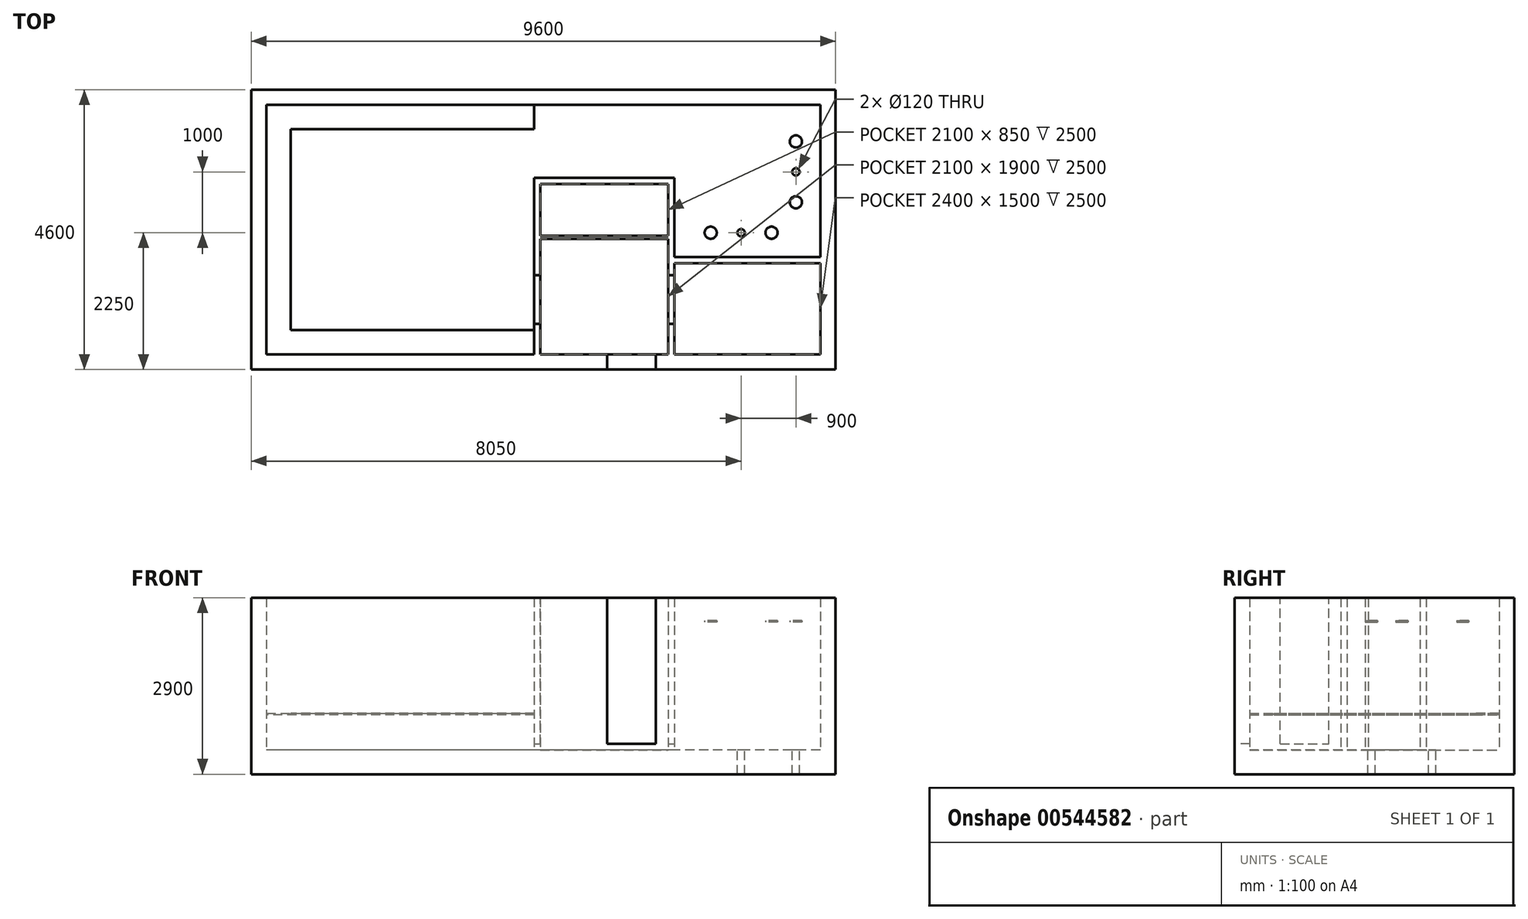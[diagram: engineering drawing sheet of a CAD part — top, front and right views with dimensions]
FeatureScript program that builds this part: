
annotation { "Feature Type Name" : "Feature", "Feature Type Description" : "" }
export const myFeature = defineFeature(function(context is Context, id is Id, definition is map)
    precondition{}
    {
        {
            var Q0;
            Q0=qCreatedBy(makeId("Top.planeOp"),FACE);
            var sketch = newSketch(context, id + "F0", { "sketchPlane" : qUnion([Q0])});
            skLineSegment(sketch, "E0.bottom", {"start": v(4550, -2050) * mm, "end": v(-4550, -2050) * mm});
            skLineSegment(sketch, "E0.top", {"start": v(4550, 2050) * mm, "end": v(-4550, 2050) * mm});
            skLineSegment(sketch, "E0.left", {"start": v(4550, -2050) * mm, "end": v(4550, 2050) * mm});
            skLineSegment(sketch, "E0.right", {"start": v(-4550, -2050) * mm, "end": v(-4550, 2050) * mm});
            skPoint(sketch, "E0.middle", {"position": v(0, 0) * mm});
            skLineSegment(sketch, "E1", {"start": v(2150, -2050) * mm, "end": v(2150, -550) * mm});
            skLineSegment(sketch, "E2", {"start": v(2150, -550) * mm, "end": v(4550, -550) * mm});
            skLineSegment(sketch, "E3", {"start": v(4550, -550) * mm, "end": v(4550, -450) * mm});
            skLineSegment(sketch, "E4", {"start": v(4550, -450) * mm, "end": v(2150, -450) * mm});
            skLineSegment(sketch, "E5", {"start": v(2150, -450) * mm, "end": v(2150, 850) * mm});
            skLineSegment(sketch, "E6", {"start": v(2150, 850) * mm, "end": v(2050, 850) * mm});
            skLineSegment(sketch, "E7", {"start": v(2050, 850) * mm, "end": v(2050, 850) * mm});
            skLineSegment(sketch, "E8", {"start": v(2050, 850) * mm, "end": v(-150, 850) * mm});
            skLineSegment(sketch, "E9", {"start": v(-150, 850) * mm, "end": v(-150, -2050) * mm});
            skLineSegment(sketch, "E10", {"start": v(-150, -2050) * mm, "end": v(-50, -2050) * mm});
            skLineSegment(sketch, "E11", {"start": v(-50, -2050) * mm, "end": v(-50, 750) * mm});
            skLineSegment(sketch, "E12", {"start": v(-50, 750) * mm, "end": v(2050, 750) * mm});
            skLineSegment(sketch, "E13", {"start": v(2050, 750) * mm, "end": v(2050, -2050) * mm});
            skLineSegment(sketch, "E14", {"start": v(2050, -2050) * mm, "end": v(2150, -2050) * mm});
            skLineSegment(sketch, "E15", {"start": v(2050, 750) * mm, "end": v(2050, 850) * mm});
            skCircle(sketch, "E16", {"center": v(2750, -50) * mm, "radius": 100 * mm, "construction": true});
            skCircle(sketch, "E17", {"center": v(3750, -50) * mm, "radius": 100 * mm, "construction": true});
            skCircle(sketch, "E18", {"center": v(4150, 450) * mm, "radius": 100 * mm, "construction": true});
            skLineSegment(sketch, "E19", {"start": v(2150, -50) * mm, "end": v(2750, -50) * mm, "construction": true});
            skLineSegment(sketch, "E20", {"start": v(3750, -50) * mm, "end": v(2750, -50) * mm, "construction": true});
            skLineSegment(sketch, "E21", {"start": v(4550, -50) * mm, "end": v(3750, -50) * mm, "construction": true});
            skLineSegment(sketch, "E22", {"start": v(3750, -50) * mm, "end": v(3750, -450) * mm, "construction": true});
            skLineSegment(sketch, "E23", {"start": v(4550, 450) * mm, "end": v(4150, 450) * mm, "construction": true});
            skCircle(sketch, "E24", {"center": v(4150, 1450) * mm, "radius": 100 * mm, "construction": true});
            skLineSegment(sketch, "E25", {"start": v(4150, 1450) * mm, "end": v(4150, 450) * mm, "construction": true});
            skLineSegment(sketch, "E26", {"start": v(4150, -450) * mm, "end": v(4150, 450) * mm, "construction": true});
            skPoint(sketch, "E26.startSnap0", {"position": v(4150, -50) * mm});
            skLineSegment(sketch, "E27", {"start": v(4150, 1450) * mm, "end": v(4150, 2050) * mm, "construction": true});
            skLineSegment(sketch, "E28.bottom", {"start": v(-4800, 2300) * mm, "end": v(4800, 2300) * mm});
            skLineSegment(sketch, "E28.top", {"start": v(-4800, -2300) * mm, "end": v(4800, -2300) * mm});
            skLineSegment(sketch, "E28.left", {"start": v(-4800, 2300) * mm, "end": v(-4800, -2300) * mm});
            skLineSegment(sketch, "E28.right", {"start": v(4800, 2300) * mm, "end": v(4800, -2300) * mm});
            skCircle(sketch, "E29", {"center": v(3250, -50) * mm, "radius": 60 * mm});
            skCircle(sketch, "E30", {"center": v(4150, 950) * mm, "radius": 60 * mm});
            skSolve(sketch);
        }
        {
            var Q0;
            {var subQ3=sQuery(id+"F0.wireOp",EDGE,"E1");Q0=makeQuery(id+"F0.imprint","IMPRINT",FACE,{"disambiguationData":[TD([[makeQuery(id+"F0.imprint","IMPRINT",EDGE,{"derivedFrom":subQ3}),-1.0]])]});}
            var Q1;
            {var subQ0=sQuery(id+"F0.wireOp",EDGE,"E11");Q1=makeQuery(id+"F0.imprint","IMPRINT",FACE,{"disambiguationData":[TD([[makeQuery(id+"F0.imprint","IMPRINT",EDGE,{"derivedFrom":subQ0}),-1.0]])]});}
            var Q2;
            {var subQ1=sQuery(id+"F0.wireOp",EDGE,"E0.left");var subQ3=sQuery(id+"F0.wireOp",EDGE,"E21");var subQ4=makeQuery(id+"F0.imprint","INTERSECT",VERTEX,{"derivedFrom":[subQ1,subQ3]});Q2=makeQuery(id+"F0.imprint","IMPRINT",FACE,{"disambiguationData":[TD([[makeQuery(id+"F0.imprint","IMPRINT",EDGE,{"disambiguationData":[TD([[subQ4,-1.0]])],"derivedFrom":subQ3}),1.0]])]});}
            var Q3;
            Q3=makeQuery(id+"F0.imprint","IMPRINT",FACE,{"disambiguationData":[TD([[makeQuery(id+"F0.imprint","IMPRINT",EDGE,{"derivedFrom":sQuery(id+"F0.wireOp",EDGE,"E8")}),1.0]])]});
            var Q4;
            {var subQ1=sQuery(id+"F0.wireOp",EDGE,"E0.left");var subQ6=sQuery(id+"F0.wireOp",EDGE,"E0.top");var subQ12=makeQuery(id+"F0.imprint","INTERSECT",VERTEX,{"derivedFrom":[subQ6,subQ1]});Q4=makeQuery(id+"F0.imprint","IMPRINT",FACE,{"disambiguationData":[TD([[makeQuery(id+"F0.imprint","IMPRINT",EDGE,{"disambiguationData":[TD([[subQ12,-1.0]])],"derivedFrom":subQ6}),1.0]])]});}
            var Q5;
            {var subQ1=sQuery(id+"F0.wireOp",EDGE,"E0.left");var subQ7=sQuery(id+"F0.wireOp",EDGE,"E21");var subQ8=makeQuery(id+"F0.imprint","INTERSECT",VERTEX,{"derivedFrom":[subQ1,subQ7]});Q5=makeQuery(id+"F0.imprint","IMPRINT",FACE,{"disambiguationData":[TD([[makeQuery(id+"F0.imprint","IMPRINT",EDGE,{"disambiguationData":[TD([[subQ8,-1.0]])],"derivedFrom":subQ1}),1.0]])]});}
            var Q6;
            Q6=makeQuery(id+"F0.imprint","IMPRINT",FACE,{"disambiguationData":[TD([[makeQuery(id+"F0.imprint","IMPRINT",EDGE,{"derivedFrom":sQuery(id+"F0.wireOp",EDGE,"E1")}),1.0]])]});
            var Q7;
            {var subQ9=sQuery(id+"F0.wireOp",EDGE,"E0.right");Q7=makeQuery(id+"F0.imprint","IMPRINT",FACE,{"disambiguationData":[TD([[makeQuery(id+"F0.imprint","IMPRINT",EDGE,{"derivedFrom":subQ9}),-1.0]])]});}
            var Q8;
            {var subQ9=sQuery(id+"F0.wireOp",EDGE,"E5");var subQ10=sQuery(id+"F0.wireOp",EDGE,"E4");var subQ11=makeQuery(id+"F0.imprint","INTERSECT",VERTEX,{"derivedFrom":[subQ10,subQ9]});Q8=makeQuery(id+"F0.imprint","IMPRINT",FACE,{"disambiguationData":[TD([[makeQuery(id+"F0.imprint","IMPRINT",EDGE,{"disambiguationData":[TD([[subQ11,1.0]])],"derivedFrom":subQ10}),-1.0]])]});}
            var Q9;
            {var subQ0=sQuery(id+"F0.wireOp",EDGE,"E19");var subQ1=sQuery(id+"F0.wireOp",EDGE,"E16");var subQ2=makeQuery(id+"F0.imprint","INTERSECT",VERTEX,{"derivedFrom":[subQ1,subQ0]});Q9=makeQuery(id+"F0.imprint","IMPRINT",FACE,{"disambiguationData":[TD([[makeQuery(id+"F0.imprint","IMPRINT",EDGE,{"disambiguationData":[TD([[subQ2,1.0]])],"derivedFrom":subQ1}),1.0]])]});}
            var Q10;
            {var subQ0=sQuery(id+"F0.wireOp",EDGE,"E19");var subQ1=sQuery(id+"F0.wireOp",EDGE,"E16");var subQ2=makeQuery(id+"F0.imprint","INTERSECT",VERTEX,{"derivedFrom":[subQ1,subQ0]});Q10=makeQuery(id+"F0.imprint","IMPRINT",FACE,{"disambiguationData":[TD([[makeQuery(id+"F0.imprint","IMPRINT",EDGE,{"disambiguationData":[TD([[subQ2,-1.0]])],"derivedFrom":subQ1}),1.0]])]});}
            var Q11;
            {var subQ0=sQuery(id+"F0.wireOp",EDGE,"E22");var subQ1=sQuery(id+"F0.wireOp",EDGE,"E4");var subQ2=makeQuery(id+"F0.imprint","INTERSECT",VERTEX,{"derivedFrom":[subQ1,subQ0]});Q11=makeQuery(id+"F0.imprint","IMPRINT",FACE,{"disambiguationData":[TD([[makeQuery(id+"F0.imprint","IMPRINT",EDGE,{"disambiguationData":[TD([[subQ2,1.0]])],"derivedFrom":subQ1}),-1.0]])]});}
            var Q12;
            {var subQ0=sQuery(id+"F0.wireOp",EDGE,"E25");var subQ1=sQuery(id+"F0.wireOp",EDGE,"E24");var subQ2=makeQuery(id+"F0.imprint","INTERSECT",VERTEX,{"derivedFrom":[subQ1,subQ0]});Q12=makeQuery(id+"F0.imprint","IMPRINT",FACE,{"disambiguationData":[TD([[makeQuery(id+"F0.imprint","IMPRINT",EDGE,{"disambiguationData":[TD([[subQ2,1.0]])],"derivedFrom":subQ1}),1.0]])]});}
            var Q13;
            {var subQ0=sQuery(id+"F0.wireOp",EDGE,"E25");var subQ1=sQuery(id+"F0.wireOp",EDGE,"E24");var subQ2=makeQuery(id+"F0.imprint","INTERSECT",VERTEX,{"derivedFrom":[subQ1,subQ0]});Q13=makeQuery(id+"F0.imprint","IMPRINT",FACE,{"disambiguationData":[TD([[makeQuery(id+"F0.imprint","IMPRINT",EDGE,{"disambiguationData":[TD([[subQ2,-1.0]])],"derivedFrom":subQ1}),1.0]])]});}
            var Q14;
            {var subQ0=sQuery(id+"F0.wireOp",EDGE,"E25");var subQ1=sQuery(id+"F0.wireOp",EDGE,"E18");var subQ2=makeQuery(id+"F0.imprint","INTERSECT",VERTEX,{"derivedFrom":[subQ1,subQ0]});Q14=makeQuery(id+"F0.imprint","IMPRINT",FACE,{"disambiguationData":[TD([[makeQuery(id+"F0.imprint","IMPRINT",EDGE,{"disambiguationData":[TD([[subQ2,-1.0]])],"derivedFrom":subQ1}),1.0]])]});}
            var Q15;
            {var subQ0=sQuery(id+"F0.wireOp",EDGE,"E25");var subQ1=sQuery(id+"F0.wireOp",EDGE,"E18");var subQ2=makeQuery(id+"F0.imprint","INTERSECT",VERTEX,{"derivedFrom":[subQ1,subQ0]});Q15=makeQuery(id+"F0.imprint","IMPRINT",FACE,{"disambiguationData":[TD([[makeQuery(id+"F0.imprint","IMPRINT",EDGE,{"disambiguationData":[TD([[subQ2,1.0]])],"derivedFrom":subQ1}),1.0]])]});}
            var Q16;
            {var subQ0=sQuery(id+"F0.wireOp",EDGE,"E21");var subQ1=sQuery(id+"F0.wireOp",EDGE,"E17");var subQ2=makeQuery(id+"F0.imprint","INTERSECT",VERTEX,{"derivedFrom":[subQ1,subQ0]});Q16=makeQuery(id+"F0.imprint","IMPRINT",FACE,{"disambiguationData":[TD([[makeQuery(id+"F0.imprint","IMPRINT",EDGE,{"disambiguationData":[TD([[subQ2,1.0]])],"derivedFrom":subQ1}),1.0]])]});}
            var Q17;
            {var subQ0=sQuery(id+"F0.wireOp",EDGE,"E20");var subQ1=sQuery(id+"F0.wireOp",EDGE,"E17");var subQ2=makeQuery(id+"F0.imprint","INTERSECT",VERTEX,{"derivedFrom":[subQ1,subQ0]});Q17=makeQuery(id+"F0.imprint","IMPRINT",FACE,{"disambiguationData":[TD([[makeQuery(id+"F0.imprint","IMPRINT",EDGE,{"disambiguationData":[TD([[subQ2,-1.0]])],"derivedFrom":subQ1}),1.0]])]});}
            var Q18;
            {var subQ0=sQuery(id+"F0.wireOp",EDGE,"E20");var subQ1=sQuery(id+"F0.wireOp",EDGE,"E17");var subQ2=makeQuery(id+"F0.imprint","INTERSECT",VERTEX,{"derivedFrom":[subQ1,subQ0]});Q18=makeQuery(id+"F0.imprint","IMPRINT",FACE,{"disambiguationData":[TD([[makeQuery(id+"F0.imprint","IMPRINT",EDGE,{"disambiguationData":[TD([[subQ2,1.0]])],"derivedFrom":subQ1}),1.0]])]});}
            var Q19;
            {var subQ0=sQuery(id+"F0.wireOp",EDGE,"E23");var subQ1=sQuery(id+"F0.wireOp",EDGE,"E18");var subQ2=makeQuery(id+"F0.imprint","INTERSECT",VERTEX,{"derivedFrom":[subQ1,subQ0]});Q19=makeQuery(id+"F0.imprint","IMPRINT",FACE,{"disambiguationData":[TD([[makeQuery(id+"F0.imprint","IMPRINT",EDGE,{"disambiguationData":[TD([[subQ2,1.0]])],"derivedFrom":subQ1}),1.0]])]});}
            var Q20;
            {var subQ0=sQuery(id+"F0.wireOp",EDGE,"E0.right");Q20=makeQuery(id+"F0.imprint","IMPRINT",FACE,{"disambiguationData":[TD([[makeQuery(id+"F0.imprint","IMPRINT",EDGE,{"derivedFrom":subQ0}),1.0]])]});}
            extrude(context, id + "F1", {"entities" : qUnion([Q0, Q1, Q2, Q3, Q4, Q5, Q6, Q7, Q8, Q9, Q10, Q11, Q12, Q13, Q14, Q15, Q16, Q17, Q18, Q19, Q20]), "oppositeDirection" : true, "depth" : 400 * mm, "offsetDistance" : 25 * mm});
        }
        {
            var Q0;
            Q0=makeQuery(id+"F0.imprint","IMPRINT",FACE,{"disambiguationData":[TD([[makeQuery(id+"F0.imprint","IMPRINT",EDGE,{"derivedFrom":sQuery(id+"F0.wireOp",EDGE,"E1")}),1.0]])]});
            var Q1;
            Q1=makeQuery(id+"F0.imprint","IMPRINT",FACE,{"disambiguationData":[TD([[makeQuery(id+"F0.imprint","IMPRINT",EDGE,{"derivedFrom":sQuery(id+"F0.wireOp",EDGE,"E8")}),1.0]])]});
            var Q2;
            {var subQ0=sQuery(id+"F0.wireOp",EDGE,"E0.right");Q2=makeQuery(id+"F0.imprint","IMPRINT",FACE,{"disambiguationData":[TD([[makeQuery(id+"F0.imprint","IMPRINT",EDGE,{"derivedFrom":subQ0}),1.0]])]});}
            extrude(context, id + "F2", {"entities" : qUnion([Q0, Q1, Q2]), "operationType" : NewBodyOperationType.ADD, "depth" : 2500 * mm, "offsetDistance" : 25 * mm});
        }
        {
            var Q0;
            {var subQ0=sQuery(id+"F0.wireOp",EDGE,"E28.top");Q0=makeQuery(id+"F2.boolean.opBoolean","MERGE",FACE,{"derivedFrom":[makeQuery(id+"F1.opExtrude","SWEPT_FACE",FACE,{"disambiguationData":[OSD([subQ0])]}),makeQuery(id+"F2.opExtrude","SWEPT_FACE",FACE,{"disambiguationData":[OSD([subQ0])]})]});}
            var sketch = newSketch(context, id + "F3", { "sketchPlane" : qUnion([Q0])});
            skLineSegment(sketch, "E31.bottom", {"start": v(1050, 2600) * mm, "end": v(1850, 2600) * mm});
            skLineSegment(sketch, "E31.top", {"start": v(1050, 100) * mm, "end": v(1850, 100) * mm});
            skLineSegment(sketch, "E31.left", {"start": v(1050, 2600) * mm, "end": v(1050, 100) * mm});
            skLineSegment(sketch, "E31.right", {"start": v(1850, 2600) * mm, "end": v(1850, 100) * mm});
            skSolve(sketch);
        }
        {
            var Q0;
            Q0 = qSketchRegion(id + "F3", true);
            extrude(context, id + "F4", {"entities" : qUnion([Q0]), "operationType" : NewBodyOperationType.REMOVE, "oppositeDirection" : true, "depth" : 400 * mm, "hasOffset" : true, "offsetDistance" : 2000 * mm});
        }
        {
            var Q0;
            Q0=makeQuery(id+"F2.opExtrude","SWEPT_FACE",FACE,{"disambiguationData":[OSD([sQuery(id+"F0.wireOp",EDGE,"E1")])]});
            var sketch = newSketch(context, id + "F5", { "sketchPlane" : qUnion([Q0])});
            skLineSegment(sketch, "E32.bottom", {"start": v(-750, 2600) * mm, "end": v(-1550, 2600) * mm});
            skLineSegment(sketch, "E32.top", {"start": v(-750, 100) * mm, "end": v(-1550, 100) * mm});
            skLineSegment(sketch, "E32.left", {"start": v(-750, 2600) * mm, "end": v(-750, 100) * mm});
            skLineSegment(sketch, "E32.right", {"start": v(-1550, 2600) * mm, "end": v(-1550, 100) * mm});
            skSolve(sketch);
        }
        {
            var Q0;
            Q0 = qSketchRegion(id + "F5", true);
            extrude(context, id + "F6", {"entities" : qUnion([Q0]), "operationType" : NewBodyOperationType.REMOVE, "oppositeDirection" : true, "depth" : 4000 * mm, "offsetDistance" : 25 * mm});
        }
        {
            var Q0;
            Q0=makeQuery(id+"F2.opExtrude","SWEPT_FACE",FACE,{"disambiguationData":[OSD([sQuery(id+"F0.wireOp",EDGE,"E11")])]});
            var sketch = newSketch(context, id + "F7", { "sketchPlane" : qUnion([Q0])});
            skLineSegment(sketch, "E33.bottom", {"start": v(-650, 2600) * mm, "end": v(-1450, 2600) * mm});
            skLineSegment(sketch, "E33.top", {"start": v(-650, 100) * mm, "end": v(-1450, 100) * mm});
            skLineSegment(sketch, "E33.left", {"start": v(-650, 2600) * mm, "end": v(-650, 100) * mm});
            skLineSegment(sketch, "E33.right", {"start": v(-1450, 2600) * mm, "end": v(-1450, 100) * mm});
            skSolve(sketch);
        }
        {
            var Q0;
            Q0=qCreatedBy(makeId("Top.planeOp"),FACE);
            cPlane(context, id + "F8", {"entities" : qUnion([Q0]), "cplaneType" : CPlaneType.OFFSET, "offset" : 600 * mm, "width" : 150 * mm, "height" : 150 * mm});
        }
        {
            var Q0;
            Q0=qCreatedBy(id+"F8.planeOp",FACE);
            var sketch = newSketch(context, id + "F9", { "sketchPlane" : qUnion([Q0])});
            skLineSegment(sketch, "E34", {"start": v(-4550, -2050) * mm, "end": v(-4550, 2050) * mm});
            skLineSegment(sketch, "E35", {"start": v(-4550, 2050) * mm, "end": v(-150, 2050) * mm});
            skLineSegment(sketch, "E36", {"start": v(-4550, -2050) * mm, "end": v(-150, -2050) * mm});
            skSolve(sketch);
        }
        {
            var Q0;
            Q0=makeQuery(id+"F2.opExtrude","SWEPT_FACE",FACE,{"disambiguationData":[OSD([sQuery(id+"F0.wireOp",EDGE,"E9")])]});
            var sketch = newSketch(context, id + "F10", { "sketchPlane" : qUnion([Q0])});
            skLineSegment(sketch, "E37.bottom", {"start": v(2050, 575) * mm, "end": v(1650, 575) * mm});
            skLineSegment(sketch, "E37.top", {"start": v(2050, 600) * mm, "end": v(1650, 600) * mm});
            skLineSegment(sketch, "E37.left", {"start": v(2050, 575) * mm, "end": v(2050, 600) * mm});
            skLineSegment(sketch, "E37.right", {"start": v(1650, 575) * mm, "end": v(1650, 600) * mm});
            skPoint(sketch, "E37.middle", {"position": v(1850, 587.5) * mm});
            skSolve(sketch);
        }
        {
            var Q0;
            Q0 = qSketchRegion(id + "F10", true);
            var Q1;
            Q1=sQuery(id+"F9.wireOp",EDGE,"E36");
            var Q2;
            Q2=sQuery(id+"F9.wireOp",EDGE,"E34");
            var Q3;
            Q3=sQuery(id+"F9.wireOp",EDGE,"E35");
            sweep(context, id + "F11", {"profiles" : qUnion([Q0]), "path" : qUnion([Q1, Q2, Q3])});
        }
        {
            var Q0;
            Q0=qCreatedBy(makeId("Top.planeOp"),FACE);
            cPlane(context, id + "F12", {"entities" : qUnion([Q0]), "cplaneType" : CPlaneType.OFFSET, "offset" : 2100 * mm, "width" : 150 * mm, "height" : 150 * mm});
        }
        {
            var Q0;
            Q0=qCreatedBy(id+"F12.planeOp",FACE);
            var sketch = newSketch(context, id + "F13", { "sketchPlane" : qUnion([Q0])});
            skCircle(sketch, "E38", {"center": v(2750, -50) * mm, "radius": 100 * mm});
            skCircle(sketch, "E39", {"center": v(4150, 1450) * mm, "radius": 100 * mm});
            skCircle(sketch, "E40", {"center": v(4150, 450) * mm, "radius": 100 * mm});
            skCircle(sketch, "E41", {"center": v(3750, -50) * mm, "radius": 100 * mm});
            skSolve(sketch);
        }
        {
            var Q0;
            Q0 = qSketchRegion(id + "F13", true);
            extrude(context, id + "F14", {"entities" : qUnion([Q0]), "depth" : 25 * mm, "offsetDistance" : 25 * mm});
        }
        {
            var Q0;
            {var subQ0=sQuery(id+"F0.wireOp",EDGE,"E11");var subQ4=sQuery(id+"F0.wireOp",EDGE,"E24");var subQ5=sQuery(id+"F0.wireOp",EDGE,"E18");var subQ6=sQuery(id+"F0.wireOp",EDGE,"E17");var subQ7=sQuery(id+"F0.wireOp",EDGE,"E16");var subQ8=makeQuery(id+"F1.opExtrude","CAP_FACE",FACE,{"disambiguationData":[OSD([subQ7,subQ6,subQ5,subQ4,sQuery(id+"F0.wireOp",EDGE,"E28.bottom"),sQuery(id+"F0.wireOp",EDGE,"E28.top"),sQuery(id+"F0.wireOp",EDGE,"E28.left"),sQuery(id+"F0.wireOp",EDGE,"E28.right")])],"isStart":true});Q0=makeQuery(id+"FE00BlGjjyCxvcy_1.boolean.opBoolean","MERGE",FACE,{"derivedFrom":[makeQuery(id+"F2.boolean.opBoolean","SPLIT",FACE,{"disambiguationData":[TD([makeQuery(id+"F1.opExtrude","SWEPT_FACE",FACE,{"disambiguationData":[OSD([subQ7])]})])],"derivedFrom":subQ8}),makeQuery(id+"F2.boolean.opBoolean","SPLIT",FACE,{"disambiguationData":[TD([makeQuery(id+"F2.opExtrude","SWEPT_FACE",FACE,{"disambiguationData":[OSD([subQ0])]})])],"derivedFrom":subQ8}),makeQuery(id+"FE00BlGjjyCxvcy_1.opExtrude","SWEPT_FACE",FACE,{"disambiguationData":[OSD([sQuery(id+"F7.wireOp",EDGE,"E33.top")])]})]});}
            var sketch = newSketch(context, id + "F15", { "sketchPlane" : qUnion([Q0])});
            skLineSegment(sketch, "E42.bottom", {"start": v(-50, 750) * mm, "end": v(2050, 750) * mm, "construction": true});
            skLineSegment(sketch, "E42.top", {"start": v(-50, -150) * mm, "end": v(2050, -150) * mm, "construction": true});
            skLineSegment(sketch, "E42.left", {"start": v(-50, 750) * mm, "end": v(-50, -150) * mm, "construction": true});
            skLineSegment(sketch, "E42.right", {"start": v(2050, 750) * mm, "end": v(2050, -150) * mm, "construction": true});
            skLineSegment(sketch, "E43.bottom", {"start": v(-50, -150) * mm, "end": v(2050, -150) * mm});
            skLineSegment(sketch, "E43.top", {"start": v(-50, -100) * mm, "end": v(2050, -100) * mm});
            skLineSegment(sketch, "E43.left", {"start": v(-50, -150) * mm, "end": v(-50, -100) * mm});
            skLineSegment(sketch, "E43.right", {"start": v(2050, -150) * mm, "end": v(2050, -100) * mm});
            skSolve(sketch);
        }
        {
            var Q0;
            Q0 = qSketchRegion(id + "F15", true);
            extrude(context, id + "F16", {"entities" : qUnion([Q0]), "operationType" : NewBodyOperationType.ADD, "depth" : 2500 * mm, "offsetDistance" : 25 * mm});
        }
    });
